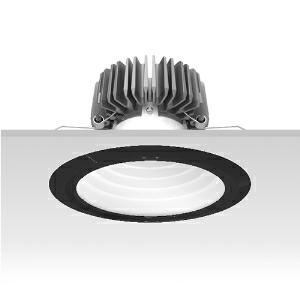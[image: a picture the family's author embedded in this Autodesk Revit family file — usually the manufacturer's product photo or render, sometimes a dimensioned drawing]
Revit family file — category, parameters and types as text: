
# Revit family: 3f_filippi_-_3f_reno_bianco_ampio_3f_filippi_-_30683_a01026_-_3f_reno_200_wh_3000-930_dali_wide___vt_bk_4772
name_source: partatom
category: Lighting Fixtures
units: mm (PartAtom-declared; Revit-internal decimal feet)

## family parameters
Cut with Voids When Loaded = No
Host = Face
Light Source = No
Part Type = Normal
Room Calculation Point = No
Round Connector Dimension = Use Diameter
Shared = No

## types (1)
- 3F Filippi - 3F Reno Bianco Ampio (1 x LED, 2537 lm, 37 W, 3000 K)
    Apparent Load = 37 VA
    Approval mark = CE
    CIE Flux Codes = 75 94 99 100 100
    Color Rendering = 90
    Color Temperature = 3000 K
    Control Gear = Electronic transformer
    Default Elevation = 1800 mm
    Description = ILLUMINOTECHNICAL
Luminous efficiency 100% (DLOR 100%, ULOR 0%).
Initial luminous flux of the luminaire 2537 lm.
Direct symmetric wide distribution.
Installation Interdistance Transv.D = 1.56 x hu - Long.D = 1.56 x hu.
Tabular UGR (CIE 117 - 4H-8H; S=0.25H; 70/50/20): RUG 21.8 - 21.7.
Beam angle: 74° - 74°.
Luminous efficacy 69 lm/W.
Lifetime (L90/B10): 30000 h. (tq+25°C)
Lifetime (L85/B10): 50000 h. (tq+25°C)
Lifetime (L70/B10): 80000 h. (tq+25°C)
Sudden decreased luminous flux after 50000 hours: 0% (C0).
Photobiological safety in compliance with IEC/TR 62778: RG0 risk exempt, (IEC 62471).
In compliance with IEC/EN 62722-2-1 - IEC/EN 62717 standards.

SOURCE
Compact LED module 3000/930.
Energy efficiency class (UE 2019/2020 - UE 2019/2015): E.
CIE 13.3 Colour rendering index: CRI >90 (R9 >50%).
IES TM-30 Fidelity Index: Rf = 92 Rg = 101.
CCT nominal colour temperature 3000 K.
Colour initial tolerance (MacAdam): SDCM 3.
Zhaga Book 3 compliant.

MECHANICAL
Passive heat dissipator in die-casting aluminium, oversized, for optimum thermal management of the LED module.
Parabolic element with graduated/concentric rings in white polycarbonate.
Transparent external lens with glossy and satin differentiated surfaces, with a cooling and anti-insect system in methacrylate (PMMA).
Fastening spring clips in stainless steel.
Dimensions: diameter 226 mm, height 146 mm. Weight 1.755 kg.
IP44 protection degree for exposed part, IP20 for recessed part.
Mechanical strength to impacts IK06 (1 joule).
Glow-wire test resistance 650°C.

ELECTRICAL
Wiring on a separate unit.
Halogen Free DALI-2 DATI (Parts 251, 252, 253), PUSH-DIM, electronic wiring 230V-50/60Hz, power factor 0.97 at full load, THD <25%, constant output current, SELV, class II, 1 driver, 1 DALI addresse.
Power of the luminaire 37 W.
ENEC - CE.
SAFE FLICKER: PstLM=<1 and SVM=<0.4 (IEC TR 61547-1 and IEC TR 63158), to ensure a more comfortable and safe light.
Luminaire compliant with EN 60598-2-22 for power supply from a centralised emergency system CPSS (Central Power Supply System), not incorporated in the luminaire - high risk areas excluded. The default power and flux are 100% in AC and 100% in DC.
Ambient temperature from 0°C to +25°C.
Temperature class T6 max 85°C.
Relative humidity UR: <85%.

INSTALLATION
Pull-up recessed fitting.
False ceiling carving: 200 mm.
All accessories dedicated to this product are available on the Catalog and on our website www.3F-Filippi.com.

ACCESSORIES
A01026 - VT transparent glass, tempered, not flammable, locked and in line with the trim, in black polycarbonate.

APPLICATIONS
Environments: architectural, commercial, exhibition areas, transit areas, corridors, shops, display windows, service areas.
In false ceilings with narrow voids.

LIGHT MANAGEMENT
Recommended minimum setting: 10%.
The luminaire, equipped with (DALI-2 DATI) driver, can be controlled manually with 3F Easy Dim technology or automatically/manually with wired or wireless DALI/D2D control systems.
The D2D driver guarantees interoperability with other devices with the same certification by making the following information available:
Device Data (Part 251), Energy Report (Part 252), Diagnosis & Maintenance (Part 253).
In electrical systems without a regulation system (manual or automatic) and DALI bus, a suitable jumper must be made on the DA-DA terminals of the appliance.

WARNING
Luminaire designed for disposal/recycling at end-of-life.
Replaceable (LED only) light source by a professional. Replaceable control gear by a professional.
    Height = 0 mm  [stored 0 ft]
    Lamp = 1 x LED
    Lamp Light Flux = 2537 lm
    Lamp Power = 37 W
    Lamp count = 1
    Length = 226 mm
    Lifetime = 50000 h
    Luminous efficacy = 69 lm/W
    Manufacturer = 3F Filippi
    ModVariant = No
    Model = 3F Filippi - 30683+A01026 - 3F Reno 200 WH 3000-930 DALI WIDE + VT BK
    Mounting Place = Ceiling
    Mounting Type = Recessed
    Number of Poles = 1
    OnlyDefault = Yes
    Power Factor = 1
    Product Name = 3F Filippi - 3F Reno Bianco Ampio
    Product group = recessed luminaire
    ProductGroupID = 4
    Protection Class = Protection class II
    Protection Degree = IP 20
    RLX_Detail_Level = 1
    RLX_Emergency_Light_Flux = 0 lm
    RLX_Emergency_Type = 0
    RLX_Emergency_Type_DB = No
    RlxData = <blob elided: 102637 chars, md5=10164d32>
    Socket = socket
    Standby Power = 0 W
    System Light Flux = 2537 lm
    System Power = 37 W
    Type Comments = Product without accessories
    Type Image = 3ffilippi_3f_reno_200_wh__a01026.jpg
    URL = http://relux.com
    VarID = ---
    Voltage = 0 V
    Weight = 0.00 kg
    Width = 0 mm  [stored 0 ft]

note: [stored X ft] marks values corroborated as IEEE doubles in the binary element streams (Revit-internal decimal feet)

## geometry (parser evidence)
native form markers: Blend x4, Sweep x9
no freeform markers — native parametric forms only
